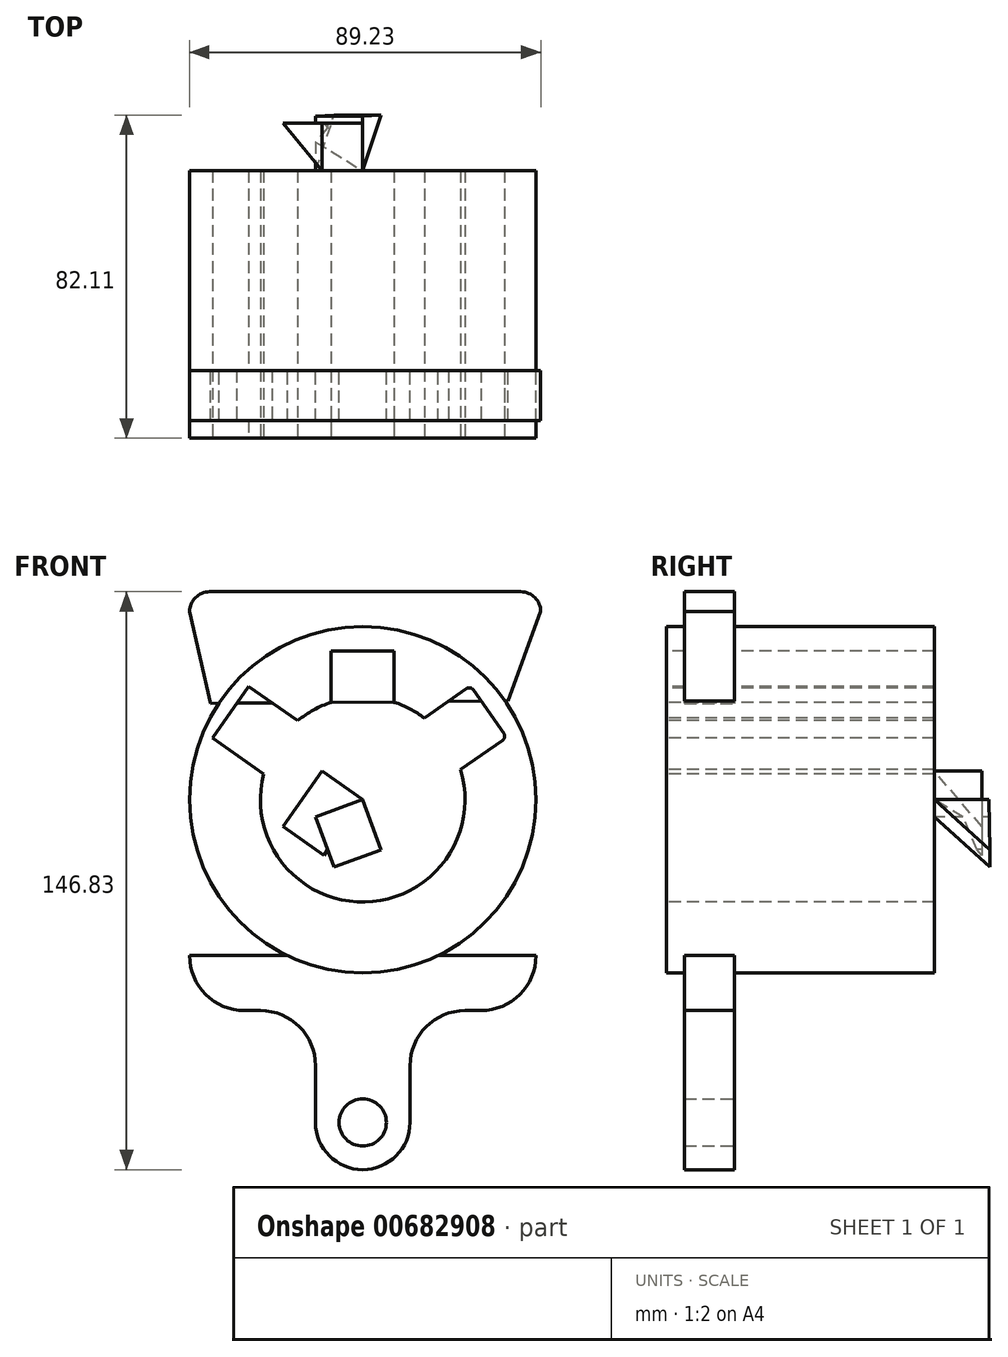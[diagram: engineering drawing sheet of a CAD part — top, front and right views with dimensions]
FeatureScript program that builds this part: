
annotation { "Feature Type Name" : "Feature", "Feature Type Description" : "" }
export const myFeature = defineFeature(function(context is Context, id is Id, definition is map)
    precondition{}
    {
        {
            var Q0;
            Q0=qCreatedBy(makeId("Front.planeOp"),FACE);
            var sketch = newSketch(context, id + "F0", { "sketchPlane" : qUnion([Q0])});
            skCircle(sketch, "E0", {"center": v(0, 0) * mm, "radius": 44 * mm});
            skLineSegment(sketch, "E1", {"start": v(0, 0) * mm, "end": v(0, 44) * mm, "construction": true});
            skLineSegment(sketch, "E2", {"start": v(0, 0) * mm, "end": v(-44, 0) * mm, "construction": true});
            skLineSegment(sketch, "E3", {"start": v(0, 0) * mm, "end": v(44, 0) * mm, "construction": true});
            skLineSegment(sketch, "E4", {"start": v(0, 0) * mm, "end": v(0, -44) * mm, "construction": true});
            skSolve(sketch);
        }
        {
            var Q0;
            Q0=makeQuery(id+"F0.imprint","IMPRINT",FACE,{"disambiguationData":[TD([[makeQuery(id+"F0.imprint","IMPRINT",EDGE,{"derivedFrom":sQuery(id+"F0.wireOp",EDGE,"E0")}),1.0]])]});
            extrude(context, id + "F1", {"entities" : qUnion([Q0]), "depth" : 68 * mm, "offsetDistance" : 25.4 * mm});
        }
        {
            var Q0;
            Q0=makeQuery(id+"F1.opExtrude","CAP_FACE",FACE,{"disambiguationData":[OSD([sQuery(id+"F0.wireOp",EDGE,"E0")])],"isStart":false});
            cPlane(context, id + "F2", {"entities" : qUnion([Q0]), "cplaneType" : CPlaneType.OFFSET, "offset" : 0 * mm, "oppositeDirection" : true, "width" : 152.4 * mm, "height" : 152.4 * mm});
        }
        {
            var Q0;
            Q0=qCreatedBy(id+"F2.planeOp",FACE);
            var sketch = newSketch(context, id + "F3", { "sketchPlane" : qUnion([Q0])});
            skArc(sketch, "E5", {"start": v(15.68, 20.74) * mm, "mid": v(-0.54, 26) * mm, "end": v(-16.52, 20.08) * mm});
            skLineSegment(sketch, "E6", {"start": v(0, 0) * mm, "end": v(93.56, 0) * mm, "construction": true});
            skLineSegment(sketch, "E7", {"start": v(0, 0) * mm, "end": v(-75.57, 0) * mm, "construction": true});
            skLineSegment(sketch, "E8", {"start": v(0, 0) * mm, "end": v(0, 26) * mm, "construction": true});
            skLineSegment(sketch, "E9", {"start": v(0, 26) * mm, "end": v(0, 37.74) * mm, "construction": true});
            skLineSegment(sketch, "E10", {"start": v(0, 37.74) * mm, "end": v(-8, 37.74) * mm});
            skLineSegment(sketch, "E11", {"start": v(0, 37.74) * mm, "end": v(8, 37.74) * mm});
            skLineSegment(sketch, "E12", {"start": v(-8, 37.74) * mm, "end": v(-8, 24.74) * mm});
            skLineSegment(sketch, "E13", {"start": v(8, 37.74) * mm, "end": v(8, 24.74) * mm});
            skLineSegment(sketch, "E14", {"start": v(28.1, 27.89) * mm, "end": v(35.82, 16.86) * mm});
            skLineSegment(sketch, "E15", {"start": v(35.5, 15.1) * mm, "end": v(24.85, 7.64) * mm});
            skPoint(sketch, "E16.visualSharp", {"position": v(32.04, 22.26) * mm});
            skArc(sketch, "E16.filletArc", {"start": v(28.1, 27.89) * mm, "mid": v(27.28, 28.41) * mm, "end": v(26.33, 28.2) * mm});
            skPoint(sketch, "E17.visualSharp", {"position": v(36.55, 15.82) * mm});
            skArc(sketch, "E17.filletArc", {"start": v(35.5, 15.1) * mm, "mid": v(36.03, 15.91) * mm, "end": v(35.82, 16.86) * mm});
            skLineSegment(sketch, "E18", {"start": v(0, 0) * mm, "end": v(0, -42.57) * mm, "construction": true});
            skLineSegment(sketch, "E19", {"start": v(0, 0) * mm, "end": v(15.07, -41.4) * mm, "construction": true});
            skLineSegment(sketch, "E20", {"start": v(0, 0) * mm, "end": v(-25.1, -35.85) * mm, "construction": true});
            skLineSegment(sketch, "E21", {"start": v(-29.01, 28.82) * mm, "end": v(-38.2, 15.72) * mm});
            skLineSegment(sketch, "E22", {"start": v(-38.2, 15.72) * mm, "end": v(-25.15, 6.59) * mm});
            skLineSegment(sketch, "E23", {"start": v(26.33, 28.2) * mm, "end": v(15.68, 20.74) * mm});
            skLineSegment(sketch, "E24", {"start": v(-29.01, 28.82) * mm, "end": v(-16.52, 20.08) * mm});
            skArc(sketch, "E25.trimOffspring", {"start": v(-25.15, 6.59) * mm, "mid": v(0.55, -26) * mm, "end": v(24.85, 7.64) * mm});
            skSolve(sketch);
        }
        {
            var Q0;
            Q0=qCreatedBy(makeId("Top.planeOp"),FACE);
            cPlane(context, id + "F4", {"entities" : qUnion([Q0]), "cplaneType" : CPlaneType.OFFSET, "offset" : 44.45 * mm, "oppositeDirection" : true, "width" : 152.4 * mm, "height" : 152.4 * mm});
        }
        {
            var Q0;
            Q0=qCreatedBy(makeId("Front.planeOp"),FACE);
            cPlane(context, id + "F5", {"entities" : qUnion([Q0]), "cplaneType" : CPlaneType.OFFSET, "offset" : 50.8 * mm, "width" : 152.4 * mm, "height" : 152.4 * mm});
        }
        {
            var Q0;
            Q0=qCreatedBy(id+"F5.planeOp",FACE);
            var sketch = newSketch(context, id + "F6", { "sketchPlane" : qUnion([Q0])});
            skLineSegment(sketch, "E26", {"start": v(0, 0) * mm, "end": v(0, -82) * mm});
            skCircle(sketch, "E27", {"center": v(0, -82) * mm, "radius": 6 * mm});
            skArc(sketch, "E28", {"start": v(0, -94) * mm, "mid": v(8.49, -90.49) * mm, "end": v(12, -82) * mm});
            skArc(sketch, "E29", {"start": v(0, -94) * mm, "mid": v(-8.49, -90.49) * mm, "end": v(-12, -82) * mm});
            skLineSegment(sketch, "E30", {"start": v(-12, -82) * mm, "end": v(-12, -67.59) * mm});
            skLineSegment(sketch, "E31", {"start": v(12, -82) * mm, "end": v(12, -67.59) * mm});
            skLineSegment(sketch, "E32", {"start": v(26, -53.59) * mm, "end": v(30, -53.59) * mm});
            skLineSegment(sketch, "E33", {"start": v(-26, -53.59) * mm, "end": v(-30, -53.59) * mm});
            skPoint(sketch, "E34.visualSharp", {"position": v(-47.3, -53.59) * mm});
            skArc(sketch, "E34.filletArc", {"start": v(-44, -39.62) * mm, "mid": v(-39.9, -49.5) * mm, "end": v(-30, -53.59) * mm});
            skPoint(sketch, "E35.visualSharp", {"position": v(40.48, -53.59) * mm});
            skArc(sketch, "E35.filletArc", {"start": v(30, -53.59) * mm, "mid": v(39.9, -49.5) * mm, "end": v(44, -39.62) * mm});
            skPoint(sketch, "E36.visualSharp", {"position": v(12, -53.59) * mm});
            skArc(sketch, "E36.filletArc", {"start": v(26, -53.59) * mm, "mid": v(16.1, -57.69) * mm, "end": v(12, -67.59) * mm});
            skPoint(sketch, "E37.visualSharp", {"position": v(-12, -53.59) * mm});
            skArc(sketch, "E37.filletArc", {"start": v(-12, -67.59) * mm, "mid": v(-16.1, -57.69) * mm, "end": v(-26, -53.59) * mm});
            skLineSegment(sketch, "E38", {"start": v(44, -39.62) * mm, "end": v(-44, -39.62) * mm});
            skSolve(sketch);
        }
        {
            var Q0;
            Q0=makeQuery(id+"F3.imprint","IMPRINT",FACE,{"disambiguationData":[TD([[makeQuery(id+"F3.imprint","IMPRINT",EDGE,{"derivedFrom":sQuery(id+"F3.wireOp",EDGE,"E21")}),1.0]])]});
            var Q1;
            Q1=makeQuery(id+"F3.imprint","IMPRINT",FACE,{"disambiguationData":[TD([[makeQuery(id+"F3.imprint","IMPRINT",EDGE,{"derivedFrom":sQuery(id+"F3.wireOp",EDGE,"E10")}),1.0]])]});
            var Q2;
            Q2=makeQuery(id+"F3.imprint","IMPRINT",FACE,{"disambiguationData":[TD([[makeQuery(id+"F3.imprint","IMPRINT",EDGE,{"derivedFrom":sQuery(id+"F3.wireOp",EDGE,"E14")}),-1.0]])]});
            var Q3;
            {var subQ0=sQuery(id+"F3.wireOp",EDGE,"E5");var subQ5=makeQuery(id+"F3.imprint","INTERSECT",VERTEX,{"derivedFrom":[subQ0,sQuery(id+"F3.wireOp",EDGE,"E15")]});Q3=makeQuery(id+"F3.imprint","IMPRINT",FACE,{"disambiguationData":[TD([[makeQuery(id+"F3.imprint","IMPRINT",EDGE,{"disambiguationData":[TD([[subQ5,-1.0]])],"derivedFrom":subQ0}),1.0]])]});}
            extrude(context, id + "F7", {"entities" : qUnion([Q0, Q1, Q2, Q3]), "operationType" : NewBodyOperationType.REMOVE, "endBound" : BoundingType.THROUGH_ALL, "oppositeDirection" : true, "depth" : 25.4 * mm, "offsetDistance" : 25.4 * mm});
        }
        {
            var Q0;
            Q0=qCreatedBy(makeId("Right.planeOp"),FACE);
            var Q1;
            Q1=makeQuery(id+"F1.opExtrude","CAP_EDGE",EDGE,{"disambiguationData":[OSD([sQuery(id+"F0.wireOp",EDGE,"E0")])],"isStart":false});
            cPlane(context, id + "F8", {"entities" : qUnion([Q0, Q1]), "cplaneType" : CPlaneType.LINE_ANGLE, "offset" : 25.4 * mm, "angle" : 35 * degree, "oppositeDirection" : true, "width" : 152.4 * mm, "height" : 152.4 * mm});
        }
        {
            var Q0;
            Q0=qCreatedBy(id+"F8.planeOp",FACE);
            var sketch = newSketch(context, id + "F9", { "sketchPlane" : qUnion([Q0])});
            skLineSegment(sketch, "E39", {"start": v(0, 0) * mm, "end": v(-12.07, 0) * mm});
            skLineSegment(sketch, "E40", {"start": v(-12.07, 0) * mm, "end": v(-12.07, -17.24) * mm});
            skLineSegment(sketch, "E41", {"start": v(-12.07, -17.24) * mm, "end": v(0, 0) * mm});
            skSolve(sketch);
        }
        {
            var Q0;
            Q0=makeQuery(id+"F9.imprint","IMPRINT",FACE,{"disambiguationData":[TD([[makeQuery(id+"F9.imprint","IMPRINT",EDGE,{"derivedFrom":sQuery(id+"F9.wireOp",EDGE,"E39")}),1.0]])]});
            extrude(context, id + "F10", {"entities" : qUnion([Q0]), "depth" : 12.7 * mm, "offsetDistance" : 25.4 * mm});
        }
        {
            var Q0;
            Q0=makeQuery(id+"F1.opExtrude","CAP_EDGE",EDGE,{"disambiguationData":[OSD([sQuery(id+"F0.wireOp",EDGE,"E0")])],"isStart":false});
            var Q1;
            Q1=qCreatedBy(makeId("Right.planeOp"),FACE);
            cPlane(context, id + "F11", {"entities" : qUnion([Q0, Q1]), "cplaneType" : CPlaneType.LINE_ANGLE, "offset" : 25.4 * mm, "angle" : 20 * degree, "width" : 152.4 * mm, "height" : 152.4 * mm});
        }
        {
            var Q0;
            Q0=qCreatedBy(id+"F11.planeOp",FACE);
            var sketch = newSketch(context, id + "F12", { "sketchPlane" : qUnion([Q0])});
            skLineSegment(sketch, "E42", {"start": v(-13.86, 0) * mm, "end": v(0, 0) * mm});
            skLineSegment(sketch, "E43", {"start": v(0, 0) * mm, "end": v(-14.11, -13.6) * mm});
            skLineSegment(sketch, "E44", {"start": v(-14.11, -13.6) * mm, "end": v(-13.86, 0) * mm});
            skSolve(sketch);
        }
        {
            var Q0;
            Q0=makeQuery(id+"F12.imprint","IMPRINT",FACE,{"disambiguationData":[TD([[makeQuery(id+"F12.imprint","IMPRINT",EDGE,{"derivedFrom":sQuery(id+"F12.wireOp",EDGE,"E42")}),-1.0]])]});
            extrude(context, id + "F13", {"entities" : qUnion([Q0]), "operationType" : NewBodyOperationType.ADD, "depth" : 12.7 * mm, "offsetDistance" : 25.4 * mm});
        }
        {
            var Q0;
            Q0=makeQuery(id+"F6.imprint","IMPRINT",FACE,{"disambiguationData":[TD([[makeQuery(id+"F6.imprint","IMPRINT",EDGE,{"derivedFrom":sQuery(id+"F6.wireOp",EDGE,"E27")}),-1.0]])]});
            extrude(context, id + "F14", {"entities" : qUnion([Q0]), "operationType" : NewBodyOperationType.ADD, "depth" : 12.7 * mm, "offsetDistance" : 25.4 * mm});
        }
        {
            var Q0;
            Q0=qCreatedBy(makeId("Front.planeOp"),FACE);
            cPlane(context, id + "F15", {"entities" : qUnion([Q0]), "cplaneType" : CPlaneType.OFFSET, "offset" : 50.8 * mm, "width" : 152.4 * mm, "height" : 152.4 * mm});
        }
        {
            var Q0;
            Q0=qCreatedBy(id+"F15.planeOp",FACE);
            var sketch = newSketch(context, id + "F16", { "sketchPlane" : qUnion([Q0])});
            skLineSegment(sketch, "E45", {"start": v(0, 0) * mm, "end": v(0, 52.83) * mm, "construction": true});
            skLineSegment(sketch, "E46", {"start": v(40.14, 52.83) * mm, "end": v(-38.91, 52.83) * mm});
            skPoint(sketch, "E47.visualSharp", {"position": v(45.22, 52.83) * mm});
            skArc(sketch, "E47.filletArc", {"start": v(45.22, 47.75) * mm, "mid": v(43.73, 51.35) * mm, "end": v(40.14, 52.83) * mm});
            skPoint(sketch, "E48.visualSharp", {"position": v(-44, 52.83) * mm});
            skArc(sketch, "E48.filletArc", {"start": v(-38.91, 52.83) * mm, "mid": v(-42.5, 51.35) * mm, "end": v(-44, 47.75) * mm});
            skLineSegment(sketch, "E49", {"start": v(45.22, 47.75) * mm, "end": v(36.93, 25.11) * mm});
            skLineSegment(sketch, "E50", {"start": v(-44, 47.75) * mm, "end": v(-38.66, 24.5) * mm});
            skLineSegment(sketch, "E51", {"start": v(36.93, 25.11) * mm, "end": v(-38.66, 24.5) * mm});
            skSolve(sketch);
        }
        {
            var Q0;
            Q0=makeQuery(id+"F16.imprint","IMPRINT",FACE,{"disambiguationData":[TD([[makeQuery(id+"F16.imprint","IMPRINT",EDGE,{"derivedFrom":sQuery(id+"F16.wireOp",EDGE,"E46")}),1.0]])]});
            extrude(context, id + "F17", {"entities" : qUnion([Q0]), "operationType" : NewBodyOperationType.ADD, "depth" : 12.7 * mm, "offsetDistance" : 25.4 * mm});
        }
    });
